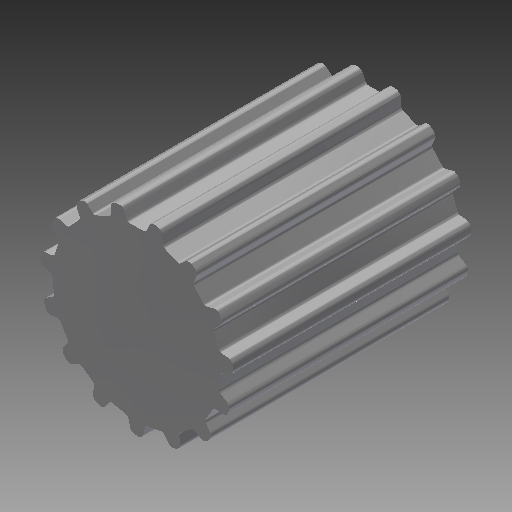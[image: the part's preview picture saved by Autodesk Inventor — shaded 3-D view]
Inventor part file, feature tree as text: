
AUTODESK INVENTOR PART (.ipt)
format: ipt  version: 2017 (Build 210142000, 142)  size: 292,352 bytes
history: native  units: mm (DEFAULTED — no unit token found)
features: other x3, extrude x2, fillet x1, pattern_circular x1
ambient origin geometry x8: Origin, YZ Plane, XZ Plane, XY Plane, X Axis, Y Axis, Z Axis, Center Point
bodies: Solid1 (feature_tree)
feature tree (7):
  other  "Pulley Sketch"
  extrude  "Base Body"  Depth=11.936621mm
  extrude  "Tooth"  Depth=0.3mm
  fillet  "Tooth Fillet"  Radius=0.75mm
  pattern_circular  "Teeth"  [2 undecoded]
  other  "Left flange"
  other  "Right flange"
note: 2 required parameter values undecoded (feature->parameter linkage not recoverable at this tier; creation-order binding heuristic only, values carry confidence <= 0.55)
